# Revit family: Electronics_Desono_Biamp_Two-Way-Pendant-Mount-Loudspeaker_P6-SM
name_source: partatom
category: Communication Devices
units: mm (PartAtom-declared; Revit-internal decimal feet)

## family parameters
Cut with Voids When Loaded = No
Host = Face
Maintain Annotation Orientation = No
OmniClass Number = 23.85.10.11.14.14.14
OmniClass Title = Loudspeakers
Part Type = Normal
Room Calculation Point = No
Round Connector Dimension = Use Diameter
Shared = No

## types (2) — shared parameters
Compliance = ETL listed to comply with UL 1480A,Certifed to CSA C22.2#62368-1 and CSA C22.2#60950-22 Cable listed to comply with UL 13, Class 3 Indoor/Outdoor rated Suspension system and Griplock cable fasteners listed per UL1598 and UL2239, TUV and CSA Class 3426-01 and Class 3426-81
Connector Description = Terminal block; Low Impedance 6 ohms, 70/100V operation
Continuous Power Handling Nominal Impedance = Passive - 19V - 60W @ 6 ohms (240W peak)
Controls = Wattage / low impedance selector switch
Default Elevation = 4' - 0"
Description = Desono™ P6-SM Two-Way 6.5-Inch Pendant Mount Loudspeaker
Diameter = 0' - 11 1/2"
Height = 0' - 5 1/2"
Input Connection = Pre-terminated inside housing
Manufacturer = Biamp
Mounting Provisions = Two pre-terminated aircraft cables (one as primary support,one as a safety cable), and Griplock cable fasteners 14 feet (4.3 m) of pre-terminated Magic Cable
Nominal Beamwidth  (H x V) = 90°, conical
Nominal Maximum SPL @ 1m = Passive - Peak 111dB - Continuous 105dB)
Nominal Sensitivity @ 1m = Passive - 1W 87dB - 2.83V 88dB)
Operating Environment = Indoor/Outdoor (splash applications only)
Operating Mode = Passive with DSP
Operating Range (-10dB) = 75 Hz to 18.5 kHz (-10dB)
Product Documentation Link = https://downloads.biamp.com
Product Page URL = https://www.biamp.com
Product data url = https://www.bimobject.com
Recommended Amplifers = 60W - 120W @ 6 ohms (19V-27V)
Required Accessories = 80 Hz, 12dB/Oct high pass flter
Shipping Weight = 29.98 lb
Transducers = LF 1 x 6.5 (165 mm) polypropylene cone; HF 1 x 1 (25 mm) soft dome
Transformer = 70V: 60W, 30W, 15W, 7.5W, 3.75W, 1.875W;100V: 60W, 30W, 15W, 7.5W, 3.75W
URL = https://www.biamp.com
Weight = 11.02 lb

## per-type parameters (varying)
| type | Bracket Material | Grill Material | Housing Material |
| P6-SM W | Biamp - Metal - White | Biamp - Plastic - White(Grid) | Biamp - Plastic - White |
| P6-SM B | Biamp - Metal - Black | Biamp - Plastic - Black(Grid) | Biamp - Plastic - Black |

note: column(s) folded — value = type name in every type: Model

## geometry (parser evidence)
native form markers: Sweep x2
no freeform markers — native parametric forms only
